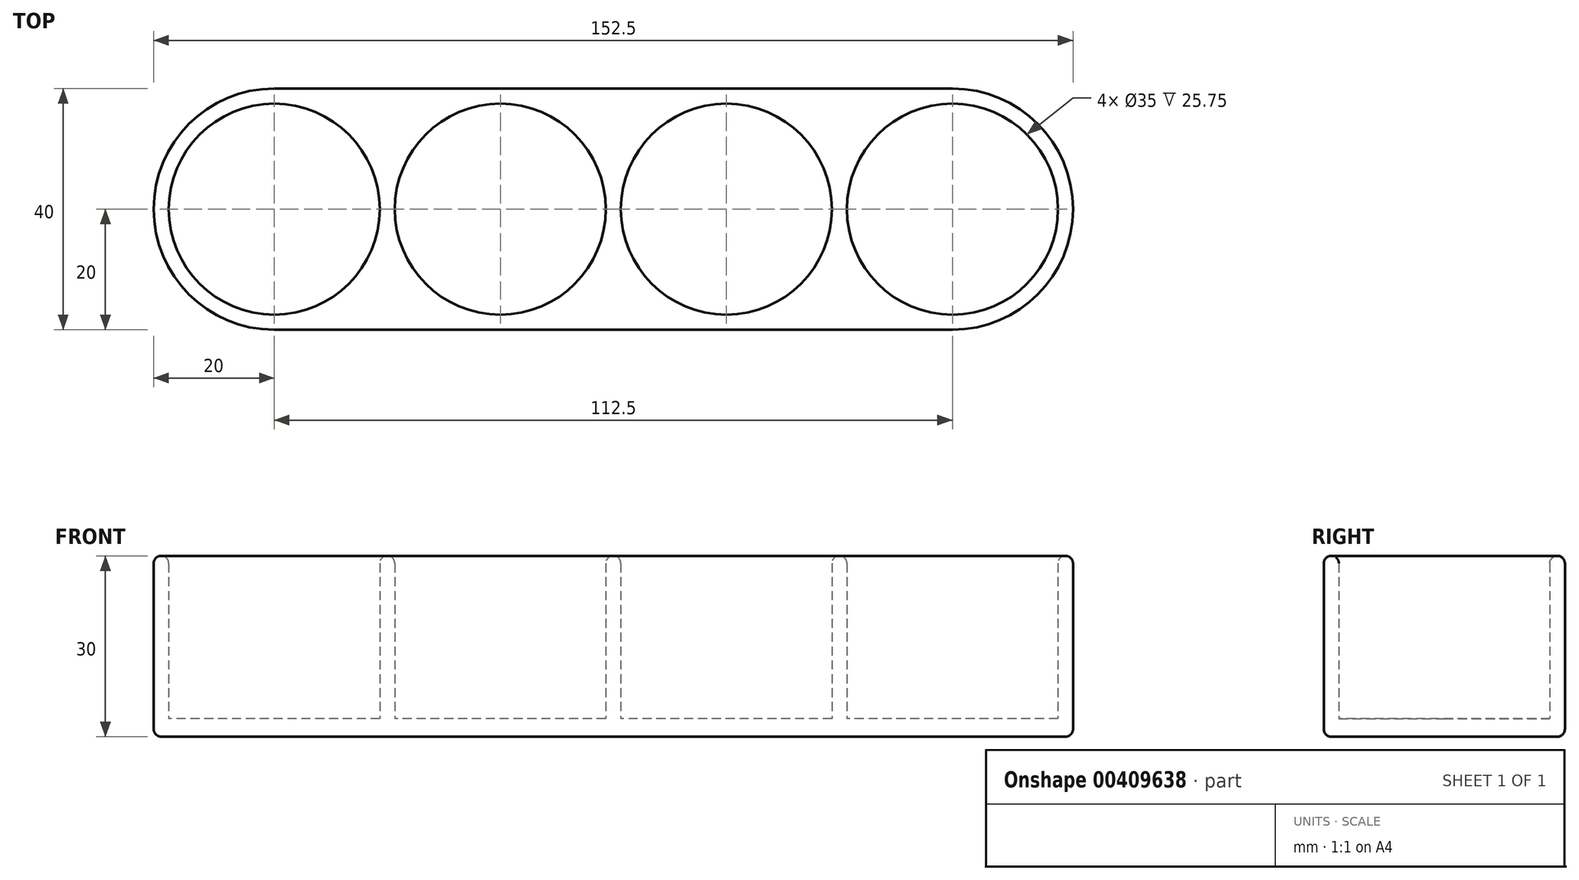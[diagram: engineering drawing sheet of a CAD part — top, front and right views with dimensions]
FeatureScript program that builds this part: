
annotation { "Feature Type Name" : "Feature", "Feature Type Description" : "" }
export const myFeature = defineFeature(function(context is Context, id is Id, definition is map)
    precondition{}
    {
        {
            var Q0;
            Q0=qCreatedBy(makeId("Top.planeOp"),FACE);
            var sketch = newSketch(context, id + "F0", { "sketchPlane" : qUnion([Q0])});
            skCircle(sketch, "E0", {"center": v(0, 0) * mm, "radius": 17.5 * mm});
            skCircle(sketch, "E1.1.0.0", {"center": v(37.5, 0) * mm, "radius": 17.5 * mm});
            skCircle(sketch, "E1.2.0.0", {"center": v(75, 0) * mm, "radius": 17.5 * mm});
            skCircle(sketch, "E1.3.0.0", {"center": v(112.5, 0) * mm, "radius": 17.5 * mm});
            skLineSegment(sketch, "E1.direction1", {"start": v(0, 0) * mm, "end": v(37.5, 0) * mm, "construction": true});
            skLineSegment(sketch, "E2.bottom", {"start": v(0, 20) * mm, "end": v(112.5, 20) * mm});
            skLineSegment(sketch, "E2.top", {"start": v(0, -20) * mm, "end": v(112.5, -20) * mm});
            skLineSegment(sketch, "E2.left", {"start": v(-20, 0) * mm, "end": v(-20, 0) * mm});
            skLineSegment(sketch, "E2.right", {"start": v(132.5, 0) * mm, "end": v(132.5, 0) * mm});
            skLineSegment(sketch, "E3", {"start": v(0, 0) * mm, "end": v(-20, 0) * mm, "construction": true});
            skPoint(sketch, "E4.visualSharp", {"position": v(-20, 20) * mm});
            skArc(sketch, "E4.filletArc", {"start": v(0, 20) * mm, "mid": v(-14.14, 14.14) * mm, "end": v(-20, 0) * mm});
            skPoint(sketch, "E5.visualSharp", {"position": v(132.5, 20) * mm});
            skArc(sketch, "E5.filletArc", {"start": v(132.5, 0) * mm, "mid": v(126.64, 14.14) * mm, "end": v(112.5, 20) * mm});
            skPoint(sketch, "E6.visualSharp", {"position": v(132.5, -20) * mm});
            skArc(sketch, "E6.filletArc", {"start": v(112.5, -20) * mm, "mid": v(126.64, -14.14) * mm, "end": v(132.5, 0) * mm});
            skPoint(sketch, "E7.visualSharp", {"position": v(-20, -20) * mm});
            skArc(sketch, "E7.filletArc", {"start": v(-20, 0) * mm, "mid": v(-14.14, -14.14) * mm, "end": v(0, -20) * mm});
            skSolve(sketch);
        }
        {
            var Q0;
            Q0=makeQuery(id+"F0.imprint","IMPRINT",FACE,{"disambiguationData":[TD([[makeQuery(id+"F0.imprint","IMPRINT",EDGE,{"derivedFrom":sQuery(id+"F0.wireOp",EDGE,"E0")}),-1.0]])]});
            extrude(context, id + "F1", {"entities" : qUnion([Q0]), "depth" : 30 * mm});
        }
        {
            var Q0;
            Q0=makeQuery(id+"F0.imprint","IMPRINT",FACE,{"disambiguationData":[TD([[makeQuery(id+"F0.imprint","IMPRINT",EDGE,{"derivedFrom":sQuery(id+"F0.wireOp",EDGE,"E0")}),1.0]])]});
            var Q1;
            Q1=makeQuery(id+"F0.imprint","IMPRINT",FACE,{"disambiguationData":[TD([[makeQuery(id+"F0.imprint","IMPRINT",EDGE,{"derivedFrom":sQuery(id+"F0.wireOp",EDGE,"E1.1.0.0")}),1.0]])]});
            var Q2;
            Q2=makeQuery(id+"F0.imprint","IMPRINT",FACE,{"disambiguationData":[TD([[makeQuery(id+"F0.imprint","IMPRINT",EDGE,{"derivedFrom":sQuery(id+"F0.wireOp",EDGE,"E1.2.0.0")}),1.0]])]});
            var Q3;
            Q3=makeQuery(id+"F0.imprint","IMPRINT",FACE,{"disambiguationData":[TD([[makeQuery(id+"F0.imprint","IMPRINT",EDGE,{"derivedFrom":sQuery(id+"F0.wireOp",EDGE,"E1.3.0.0")}),1.0]])]});
            extrude(context, id + "F2", {"entities" : qUnion([Q0, Q1, Q2, Q3]), "operationType" : NewBodyOperationType.ADD, "depth" : 3 * mm});
        }
        {
            var Q0;
            Q0=makeQuery(id+"F1.opExtrude","CAP_EDGE",EDGE,{"disambiguationData":[OSD([sQuery(id+"F0.wireOp",EDGE,"E2.top")])],"isStart":false});
            var Q1;
            Q1=makeQuery(id+"F1.opExtrude","CAP_EDGE",EDGE,{"disambiguationData":[OSD([sQuery(id+"F0.wireOp",EDGE,"E0")])],"isStart":false});
            var Q2;
            Q2=makeQuery(id+"F1.opExtrude","CAP_EDGE",EDGE,{"disambiguationData":[OSD([sQuery(id+"F0.wireOp",EDGE,"E1.1.0.0")])],"isStart":false});
            var Q3;
            Q3=makeQuery(id+"F1.opExtrude","CAP_EDGE",EDGE,{"disambiguationData":[OSD([sQuery(id+"F0.wireOp",EDGE,"E1.2.0.0")])],"isStart":false});
            var Q4;
            Q4=makeQuery(id+"F1.opExtrude","CAP_EDGE",EDGE,{"disambiguationData":[OSD([sQuery(id+"F0.wireOp",EDGE,"E1.3.0.0")])],"isStart":false});
            var Q5;
            Q5=makeQuery(id+"F1.opExtrude","CAP_EDGE",EDGE,{"disambiguationData":[OSD([sQuery(id+"F0.wireOp",EDGE,"E2.top")])],"isStart":true});
            fillet(context, id + "F3", {"entities" : qUnion([Q0, Q1, Q2, Q3, Q4, Q5]), "radius" : 1.25 * mm, "tangentPropagation" : true, "allowEdgeOverflow" : false});
        }
    });
